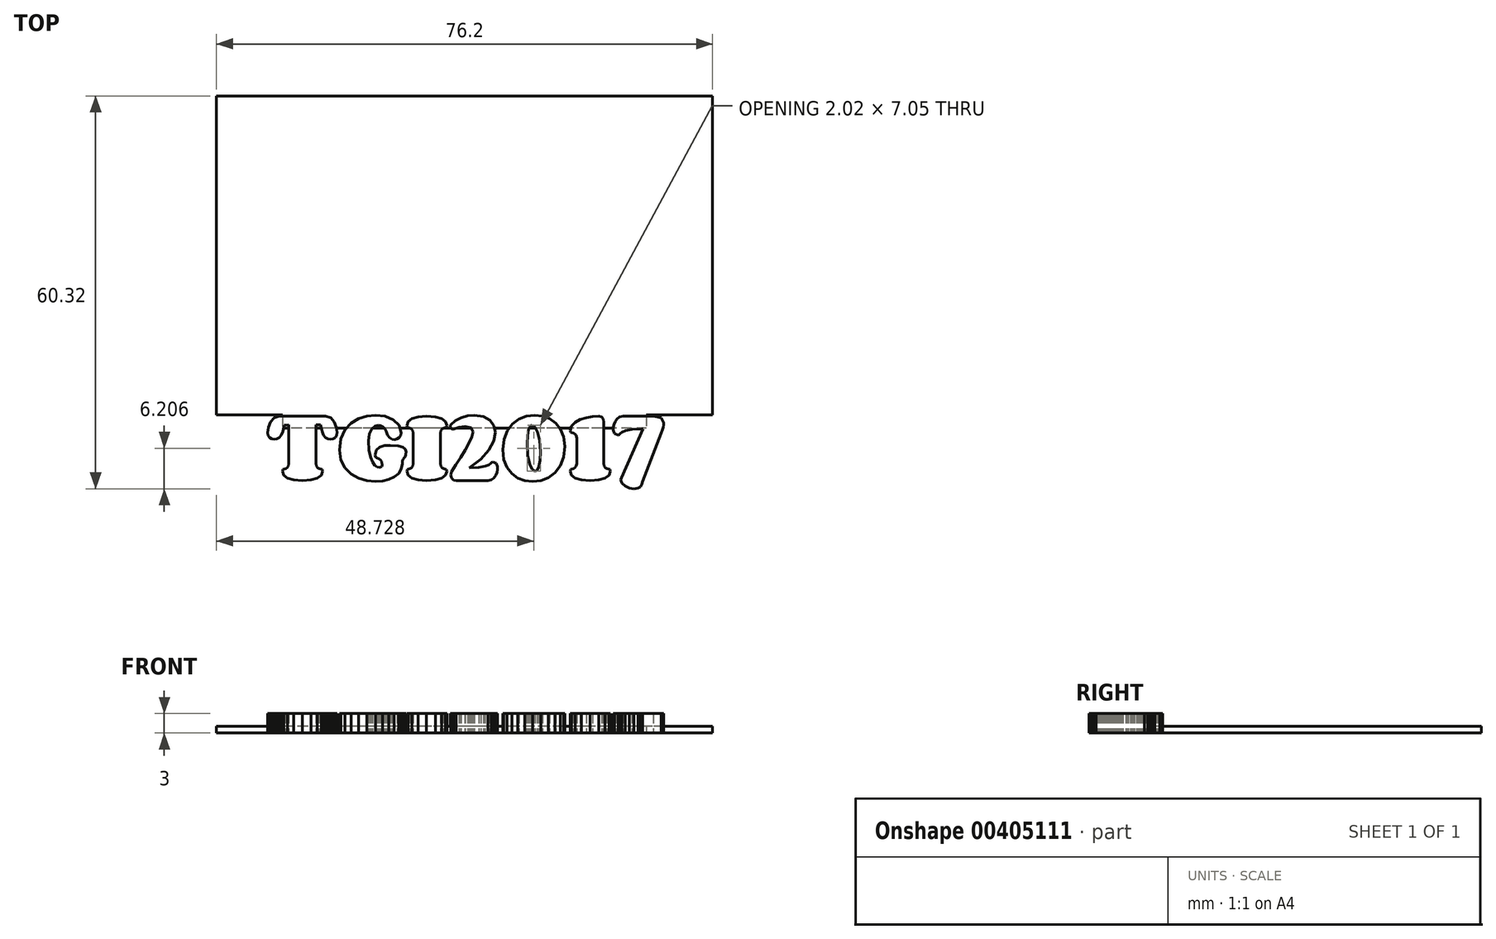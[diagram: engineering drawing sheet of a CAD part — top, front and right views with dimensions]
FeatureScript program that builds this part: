
annotation { "Feature Type Name" : "Feature", "Feature Type Description" : "" }
export const myFeature = defineFeature(function(context is Context, id is Id, definition is map)
    precondition{}
    {
        {
            var Q0;
            Q0=qCreatedBy(makeId("Top.planeOp"),FACE);
            var sketch = newSketch(context, id + "F0", { "sketchPlane" : qUnion([Q0])});
            skLineSegment(sketch, "E0.bottom", {"start": v(38.1, 24.5) * mm, "end": v(-38.1, 24.5) * mm});
            skLineSegment(sketch, "E0.top", {"start": v(38.1, -24.5) * mm, "end": v(-38.1, -24.5) * mm});
            skLineSegment(sketch, "E0.left", {"start": v(38.1, 24.5) * mm, "end": v(38.1, -24.5) * mm});
            skLineSegment(sketch, "E0.right", {"start": v(-38.1, 24.5) * mm, "end": v(-38.1, -24.5) * mm});
            skPoint(sketch, "E0.middle", {"position": v(0, 0) * mm});
            skPoint(sketch, "E1.middle", {"position": v(0, -24.5) * mm});
            skLineSegment(sketch, "E2.bottom", {"start": v(27.94, -22.5) * mm, "end": v(-27.94, -22.5) * mm});
            skLineSegment(sketch, "E2.top", {"start": v(27.94, -26.5) * mm, "end": v(-27.94, -26.5) * mm});
            skLineSegment(sketch, "E2.left", {"start": v(27.94, -22.5) * mm, "end": v(27.94, -26.5) * mm});
            skLineSegment(sketch, "E2.right", {"start": v(-27.94, -22.5) * mm, "end": v(-27.94, -26.5) * mm});
            skSolve(sketch);
        }
        {
            var Q0;
            Q0=makeQuery(id+"F0.imprint","IMPRINT",FACE,{"disambiguationData":[TD([[makeQuery(id+"F0.imprint","IMPRINT",EDGE,{"derivedFrom":sQuery(id+"F0.wireOp",EDGE,"E0.bottom")}),1.0]])]});
            var Q1;
            {var subQ5=sQuery(id+"F0.wireOp",EDGE,"E2.bottom");Q1=makeQuery(id+"F0.imprint","IMPRINT",FACE,{"disambiguationData":[TD([[makeQuery(id+"F0.imprint","IMPRINT",EDGE,{"derivedFrom":subQ5}),1.0]])]});}
            extrude(context, id + "F1", {"entities" : qUnion([Q0, Q1]), "depth" : 1 * mm});
        }
        {
            var Q0;
            {var subQ5=sQuery(id+"F0.wireOp",EDGE,"E2.top");Q0=makeQuery(id+"F0.imprint","IMPRINT",FACE,{"disambiguationData":[TD([[makeQuery(id+"F0.imprint","IMPRINT",EDGE,{"derivedFrom":subQ5}),-1.0]])]});}
            extrude(context, id + "F2", {"entities" : qUnion([Q0]), "operationType" : NewBodyOperationType.ADD, "depth" : 1 * mm});
        }
        {
            var Q0;
            Q0=qCreatedBy(makeId("Top.planeOp"),FACE);
            var sketch = newSketch(context, id + "F3", { "sketchPlane" : qUnion([Q0])});
            skLineSegment(sketch, "E3", {"start": v(-22.81, -31.93) * mm, "end": v(-22.74, -32.37) * mm});
            skLineSegment(sketch, "E4", {"start": v(-22.74, -32.37) * mm, "end": v(-22.56, -32.6) * mm});
            skLineSegment(sketch, "E5", {"start": v(-22.56, -32.6) * mm, "end": v(-22.31, -32.71) * mm});
            skLineSegment(sketch, "E6", {"start": v(-22.31, -32.71) * mm, "end": v(-22.07, -32.78) * mm});
            skLineSegment(sketch, "E7", {"start": v(-22.07, -32.78) * mm, "end": v(-21.89, -32.89) * mm});
            skLineSegment(sketch, "E8", {"start": v(-21.89, -32.89) * mm, "end": v(-21.81, -33.1) * mm});
            skLineSegment(sketch, "E9", {"start": v(-21.81, -33.1) * mm, "end": v(-22.01, -33.76) * mm});
            skLineSegment(sketch, "E10", {"start": v(-22.01, -33.76) * mm, "end": v(-22.6, -34.22) * mm});
            skLineSegment(sketch, "E11", {"start": v(-22.6, -34.22) * mm, "end": v(-23.6, -34.48) * mm});
            skLineSegment(sketch, "E12", {"start": v(-23.6, -34.48) * mm, "end": v(-24.93, -34.56) * mm});
            skLineSegment(sketch, "E13", {"start": v(-24.93, -34.56) * mm, "end": v(-26.22, -34.48) * mm});
            skLineSegment(sketch, "E14", {"start": v(-26.22, -34.48) * mm, "end": v(-27.18, -34.22) * mm});
            skLineSegment(sketch, "E15", {"start": v(-27.18, -34.22) * mm, "end": v(-27.77, -33.76) * mm});
            skLineSegment(sketch, "E16", {"start": v(-27.77, -33.76) * mm, "end": v(-27.97, -33.1) * mm});
            skLineSegment(sketch, "E17", {"start": v(-27.97, -33.1) * mm, "end": v(-27.9, -32.89) * mm});
            skLineSegment(sketch, "E18", {"start": v(-27.9, -32.89) * mm, "end": v(-27.71, -32.79) * mm});
            skLineSegment(sketch, "E19", {"start": v(-27.71, -32.79) * mm, "end": v(-27.48, -32.72) * mm});
            skLineSegment(sketch, "E20", {"start": v(-27.48, -32.72) * mm, "end": v(-27.24, -32.6) * mm});
            skLineSegment(sketch, "E21", {"start": v(-27.24, -32.6) * mm, "end": v(-27.06, -32.38) * mm});
            skLineSegment(sketch, "E22", {"start": v(-27.06, -32.38) * mm, "end": v(-26.98, -31.95) * mm});
            skLineSegment(sketch, "E23", {"start": v(-26.98, -31.95) * mm, "end": v(-26.98, -26.02) * mm});
            skLineSegment(sketch, "E24", {"start": v(-26.98, -26.02) * mm, "end": v(-27.68, -26.04) * mm});
            skLineSegment(sketch, "E25", {"start": v(-27.68, -26.04) * mm, "end": v(-27.92, -27.03) * mm});
            skLineSegment(sketch, "E26", {"start": v(-27.92, -27.03) * mm, "end": v(-28.16, -27.6) * mm});
            skLineSegment(sketch, "E27", {"start": v(-28.16, -27.6) * mm, "end": v(-28.48, -27.97) * mm});
            skLineSegment(sketch, "E28", {"start": v(-28.48, -27.97) * mm, "end": v(-28.83, -28.18) * mm});
            skLineSegment(sketch, "E29", {"start": v(-28.83, -28.18) * mm, "end": v(-29.2, -28.25) * mm});
            skLineSegment(sketch, "E30", {"start": v(-29.2, -28.25) * mm, "end": v(-29.61, -28.18) * mm});
            skLineSegment(sketch, "E31", {"start": v(-29.61, -28.18) * mm, "end": v(-29.94, -27.96) * mm});
            skLineSegment(sketch, "E32", {"start": v(-29.94, -27.96) * mm, "end": v(-30.16, -27.63) * mm});
            skLineSegment(sketch, "E33", {"start": v(-30.16, -27.63) * mm, "end": v(-30.23, -27.18) * mm});
            skLineSegment(sketch, "E34", {"start": v(-30.23, -27.18) * mm, "end": v(-30.12, -26.38) * mm});
            skLineSegment(sketch, "E35", {"start": v(-30.12, -26.38) * mm, "end": v(-29.8, -25.56) * mm});
            skLineSegment(sketch, "E36", {"start": v(-29.8, -25.56) * mm, "end": v(-29.24, -24.94) * mm});
            skLineSegment(sketch, "E37", {"start": v(-29.24, -24.94) * mm, "end": v(-28.45, -24.68) * mm});
            skLineSegment(sketch, "E38", {"start": v(-28.45, -24.68) * mm, "end": v(-21.34, -24.68) * mm});
            skLineSegment(sketch, "E39", {"start": v(-21.34, -24.68) * mm, "end": v(-20.55, -24.93) * mm});
            skLineSegment(sketch, "E40", {"start": v(-20.55, -24.93) * mm, "end": v(-20, -25.55) * mm});
            skLineSegment(sketch, "E41", {"start": v(-20, -25.55) * mm, "end": v(-19.68, -26.36) * mm});
            skLineSegment(sketch, "E42", {"start": v(-19.68, -26.36) * mm, "end": v(-19.57, -27.17) * mm});
            skLineSegment(sketch, "E43", {"start": v(-19.57, -27.17) * mm, "end": v(-19.64, -27.62) * mm});
            skLineSegment(sketch, "E44", {"start": v(-19.64, -27.62) * mm, "end": v(-19.86, -27.95) * mm});
            skLineSegment(sketch, "E45", {"start": v(-19.86, -27.95) * mm, "end": v(-20.18, -28.16) * mm});
            skLineSegment(sketch, "E46", {"start": v(-20.18, -28.16) * mm, "end": v(-20.59, -28.23) * mm});
            skLineSegment(sketch, "E47", {"start": v(-20.59, -28.23) * mm, "end": v(-20.97, -28.17) * mm});
            skLineSegment(sketch, "E48", {"start": v(-20.97, -28.17) * mm, "end": v(-21.34, -27.97) * mm});
            skLineSegment(sketch, "E49", {"start": v(-21.34, -27.97) * mm, "end": v(-21.66, -27.59) * mm});
            skLineSegment(sketch, "E50", {"start": v(-21.66, -27.59) * mm, "end": v(-21.87, -27.02) * mm});
            skLineSegment(sketch, "E51", {"start": v(-21.87, -27.02) * mm, "end": v(-22.11, -26.03) * mm});
            skLineSegment(sketch, "E52", {"start": v(-22.11, -26.03) * mm, "end": v(-22.81, -26) * mm});
            skLineSegment(sketch, "E53", {"start": v(-22.81, -26) * mm, "end": v(-22.81, -31.93) * mm});
            skLineSegment(sketch, "E54", {"start": v(-9.55, -31.95) * mm, "end": v(-9.7, -32.8) * mm});
            skLineSegment(sketch, "E55", {"start": v(-9.7, -32.8) * mm, "end": v(-10.14, -33.48) * mm});
            skLineSegment(sketch, "E56", {"start": v(-10.14, -33.48) * mm, "end": v(-10.8, -34.02) * mm});
            skLineSegment(sketch, "E57", {"start": v(-10.8, -34.02) * mm, "end": v(-11.64, -34.4) * mm});
            skLineSegment(sketch, "E58", {"start": v(-11.64, -34.4) * mm, "end": v(-12.6, -34.63) * mm});
            skLineSegment(sketch, "E59", {"start": v(-12.6, -34.63) * mm, "end": v(-13.66, -34.72) * mm});
            skLineSegment(sketch, "E60", {"start": v(-13.66, -34.72) * mm, "end": v(-14.98, -34.59) * mm});
            skLineSegment(sketch, "E61", {"start": v(-14.98, -34.59) * mm, "end": v(-16.27, -34.21) * mm});
            skLineSegment(sketch, "E62", {"start": v(-16.27, -34.21) * mm, "end": v(-17.43, -33.56) * mm});
            skLineSegment(sketch, "E63", {"start": v(-17.43, -33.56) * mm, "end": v(-18.37, -32.63) * mm});
            skLineSegment(sketch, "E64", {"start": v(-18.37, -32.63) * mm, "end": v(-19, -31.4) * mm});
            skLineSegment(sketch, "E65", {"start": v(-19, -31.4) * mm, "end": v(-19.23, -29.86) * mm});
            skLineSegment(sketch, "E66", {"start": v(-19.23, -29.86) * mm, "end": v(-19, -28.15) * mm});
            skLineSegment(sketch, "E67", {"start": v(-19, -28.15) * mm, "end": v(-18.37, -26.79) * mm});
            skLineSegment(sketch, "E68", {"start": v(-18.37, -26.79) * mm, "end": v(-17.44, -25.76) * mm});
            skLineSegment(sketch, "E69", {"start": v(-17.44, -25.76) * mm, "end": v(-16.29, -25.06) * mm});
            skLineSegment(sketch, "E70", {"start": v(-16.29, -25.06) * mm, "end": v(-15.01, -24.65) * mm});
            skLineSegment(sketch, "E71", {"start": v(-15.01, -24.65) * mm, "end": v(-13.7, -24.51) * mm});
            skLineSegment(sketch, "E72", {"start": v(-13.7, -24.51) * mm, "end": v(-12.2, -24.7) * mm});
            skLineSegment(sketch, "E73", {"start": v(-12.2, -24.7) * mm, "end": v(-10.93, -25.23) * mm});
            skLineSegment(sketch, "E74", {"start": v(-10.93, -25.23) * mm, "end": v(-10.06, -26.07) * mm});
            skLineSegment(sketch, "E75", {"start": v(-10.06, -26.07) * mm, "end": v(-9.73, -27.2) * mm});
            skLineSegment(sketch, "E76", {"start": v(-9.73, -27.2) * mm, "end": v(-9.8, -27.64) * mm});
            skLineSegment(sketch, "E77", {"start": v(-9.8, -27.64) * mm, "end": v(-10.03, -27.97) * mm});
            skLineSegment(sketch, "E78", {"start": v(-10.03, -27.97) * mm, "end": v(-10.35, -28.19) * mm});
            skLineSegment(sketch, "E79", {"start": v(-10.35, -28.19) * mm, "end": v(-10.76, -28.26) * mm});
            skLineSegment(sketch, "E80", {"start": v(-10.76, -28.26) * mm, "end": v(-11.15, -28.2) * mm});
            skLineSegment(sketch, "E81", {"start": v(-11.15, -28.2) * mm, "end": v(-11.51, -28) * mm});
            skLineSegment(sketch, "E82", {"start": v(-11.51, -28) * mm, "end": v(-11.82, -27.62) * mm});
            skLineSegment(sketch, "E83", {"start": v(-11.82, -27.62) * mm, "end": v(-12.04, -27.04) * mm});
            skLineSegment(sketch, "E84", {"start": v(-12.04, -27.04) * mm, "end": v(-12.23, -26.62) * mm});
            skLineSegment(sketch, "E85", {"start": v(-12.23, -26.62) * mm, "end": v(-12.55, -26.3) * mm});
            skLineSegment(sketch, "E86", {"start": v(-12.55, -26.3) * mm, "end": v(-12.91, -26.12) * mm});
            skLineSegment(sketch, "E87", {"start": v(-12.91, -26.12) * mm, "end": v(-13.25, -26.05) * mm});
            skLineSegment(sketch, "E88", {"start": v(-13.25, -26.05) * mm, "end": v(-13.74, -26.2) * mm});
            skLineSegment(sketch, "E89", {"start": v(-13.74, -26.2) * mm, "end": v(-14.23, -26.63) * mm});
            skLineSegment(sketch, "E90", {"start": v(-14.23, -26.63) * mm, "end": v(-14.6, -27.38) * mm});
            skLineSegment(sketch, "E91", {"start": v(-14.6, -27.38) * mm, "end": v(-14.76, -28.45) * mm});
            skLineSegment(sketch, "E92", {"start": v(-14.76, -28.45) * mm, "end": v(-14.68, -29.9) * mm});
            skLineSegment(sketch, "E93", {"start": v(-14.68, -29.9) * mm, "end": v(-14.45, -30.97) * mm});
            skLineSegment(sketch, "E94", {"start": v(-14.45, -30.97) * mm, "end": v(-14.14, -31.73) * mm});
            skLineSegment(sketch, "E95", {"start": v(-14.14, -31.73) * mm, "end": v(-13.78, -32.2) * mm});
            skLineSegment(sketch, "E96", {"start": v(-13.78, -32.2) * mm, "end": v(-13.4, -32.46) * mm});
            skLineSegment(sketch, "E97", {"start": v(-13.4, -32.46) * mm, "end": v(-13.06, -32.53) * mm});
            skLineSegment(sketch, "E98", {"start": v(-13.06, -32.53) * mm, "end": v(-12.75, -32.44) * mm});
            skLineSegment(sketch, "E99", {"start": v(-12.75, -32.44) * mm, "end": v(-12.62, -32.24) * mm});
            skLineSegment(sketch, "E100", {"start": v(-12.62, -32.24) * mm, "end": v(-12.71, -31.68) * mm});
            skLineSegment(sketch, "E101", {"start": v(-12.71, -31.68) * mm, "end": v(-12.92, -31.37) * mm});
            skLineSegment(sketch, "E102", {"start": v(-12.92, -31.37) * mm, "end": v(-13.2, -31.22) * mm});
            skLineSegment(sketch, "E103", {"start": v(-13.2, -31.22) * mm, "end": v(-13.47, -31.11) * mm});
            skLineSegment(sketch, "E104", {"start": v(-13.47, -31.11) * mm, "end": v(-13.67, -30.95) * mm});
            skLineSegment(sketch, "E105", {"start": v(-13.67, -30.95) * mm, "end": v(-13.76, -30.63) * mm});
            skLineSegment(sketch, "E106", {"start": v(-13.76, -30.63) * mm, "end": v(-13.56, -29.85) * mm});
            skLineSegment(sketch, "E107", {"start": v(-13.56, -29.85) * mm, "end": v(-13.03, -29.4) * mm});
            skLineSegment(sketch, "E108", {"start": v(-13.03, -29.4) * mm, "end": v(-12.28, -29.2) * mm});
            skLineSegment(sketch, "E109", {"start": v(-12.28, -29.2) * mm, "end": v(-11.4, -29.15) * mm});
            skLineSegment(sketch, "E110", {"start": v(-11.4, -29.15) * mm, "end": v(-10.21, -29.23) * mm});
            skLineSegment(sketch, "E111", {"start": v(-10.21, -29.23) * mm, "end": v(-9.46, -29.42) * mm});
            skLineSegment(sketch, "E112", {"start": v(-9.46, -29.42) * mm, "end": v(-9.08, -29.73) * mm});
            skLineSegment(sketch, "E113", {"start": v(-9.08, -29.73) * mm, "end": v(-8.97, -30.1) * mm});
            skLineSegment(sketch, "E114", {"start": v(-8.97, -30.1) * mm, "end": v(-9.01, -30.58) * mm});
            skLineSegment(sketch, "E115", {"start": v(-9.01, -30.58) * mm, "end": v(-9.12, -30.87) * mm});
            skLineSegment(sketch, "E116", {"start": v(-9.12, -30.87) * mm, "end": v(-9.26, -31.06) * mm});
            skLineSegment(sketch, "E117", {"start": v(-9.26, -31.06) * mm, "end": v(-9.4, -31.24) * mm});
            skLineSegment(sketch, "E118", {"start": v(-9.4, -31.24) * mm, "end": v(-9.51, -31.5) * mm});
            skLineSegment(sketch, "E119", {"start": v(-9.51, -31.5) * mm, "end": v(-9.55, -31.95) * mm});
            skLineSegment(sketch, "E120", {"start": v(-3.72, -31.93) * mm, "end": v(-3.65, -32.37) * mm});
            skLineSegment(sketch, "E121", {"start": v(-3.65, -32.37) * mm, "end": v(-3.46, -32.6) * mm});
            skLineSegment(sketch, "E122", {"start": v(-3.46, -32.6) * mm, "end": v(-3.22, -32.71) * mm});
            skLineSegment(sketch, "E123", {"start": v(-3.22, -32.71) * mm, "end": v(-2.98, -32.78) * mm});
            skLineSegment(sketch, "E124", {"start": v(-2.98, -32.78) * mm, "end": v(-2.8, -32.89) * mm});
            skLineSegment(sketch, "E125", {"start": v(-2.8, -32.89) * mm, "end": v(-2.72, -33.1) * mm});
            skLineSegment(sketch, "E126", {"start": v(-2.72, -33.1) * mm, "end": v(-2.92, -33.76) * mm});
            skLineSegment(sketch, "E127", {"start": v(-2.92, -33.76) * mm, "end": v(-3.52, -34.22) * mm});
            skLineSegment(sketch, "E128", {"start": v(-3.52, -34.22) * mm, "end": v(-4.5, -34.48) * mm});
            skLineSegment(sketch, "E129", {"start": v(-4.5, -34.48) * mm, "end": v(-5.83, -34.56) * mm});
            skLineSegment(sketch, "E130", {"start": v(-5.83, -34.56) * mm, "end": v(-7.13, -34.48) * mm});
            skLineSegment(sketch, "E131", {"start": v(-7.13, -34.48) * mm, "end": v(-8.09, -34.22) * mm});
            skLineSegment(sketch, "E132", {"start": v(-8.09, -34.22) * mm, "end": v(-8.68, -33.76) * mm});
            skLineSegment(sketch, "E133", {"start": v(-8.68, -33.76) * mm, "end": v(-8.87, -33.1) * mm});
            skLineSegment(sketch, "E134", {"start": v(-8.87, -33.1) * mm, "end": v(-8.8, -32.89) * mm});
            skLineSegment(sketch, "E135", {"start": v(-8.8, -32.89) * mm, "end": v(-8.62, -32.79) * mm});
            skLineSegment(sketch, "E136", {"start": v(-8.62, -32.79) * mm, "end": v(-8.38, -32.72) * mm});
            skLineSegment(sketch, "E137", {"start": v(-8.38, -32.72) * mm, "end": v(-8.15, -32.6) * mm});
            skLineSegment(sketch, "E138", {"start": v(-8.15, -32.6) * mm, "end": v(-7.96, -32.38) * mm});
            skLineSegment(sketch, "E139", {"start": v(-7.96, -32.38) * mm, "end": v(-7.89, -31.95) * mm});
            skLineSegment(sketch, "E140", {"start": v(-7.89, -31.95) * mm, "end": v(-7.89, -27.28) * mm});
            skLineSegment(sketch, "E141", {"start": v(-7.89, -27.28) * mm, "end": v(-7.96, -26.86) * mm});
            skLineSegment(sketch, "E142", {"start": v(-7.96, -26.86) * mm, "end": v(-8.15, -26.63) * mm});
            skLineSegment(sketch, "E143", {"start": v(-8.15, -26.63) * mm, "end": v(-8.38, -26.52) * mm});
            skLineSegment(sketch, "E144", {"start": v(-8.38, -26.52) * mm, "end": v(-8.62, -26.45) * mm});
            skLineSegment(sketch, "E145", {"start": v(-8.62, -26.45) * mm, "end": v(-8.8, -26.35) * mm});
            skLineSegment(sketch, "E146", {"start": v(-8.8, -26.35) * mm, "end": v(-8.87, -26.14) * mm});
            skLineSegment(sketch, "E147", {"start": v(-8.87, -26.14) * mm, "end": v(-8.68, -25.48) * mm});
            skLineSegment(sketch, "E148", {"start": v(-8.68, -25.48) * mm, "end": v(-8.09, -25.03) * mm});
            skLineSegment(sketch, "E149", {"start": v(-8.09, -25.03) * mm, "end": v(-7.13, -24.77) * mm});
            skLineSegment(sketch, "E150", {"start": v(-7.13, -24.77) * mm, "end": v(-5.83, -24.68) * mm});
            skLineSegment(sketch, "E151", {"start": v(-5.83, -24.68) * mm, "end": v(-4.5, -24.77) * mm});
            skLineSegment(sketch, "E152", {"start": v(-4.5, -24.77) * mm, "end": v(-3.52, -25.03) * mm});
            skLineSegment(sketch, "E153", {"start": v(-3.52, -25.03) * mm, "end": v(-2.92, -25.48) * mm});
            skLineSegment(sketch, "E154", {"start": v(-2.92, -25.48) * mm, "end": v(-2.72, -26.14) * mm});
            skLineSegment(sketch, "E155", {"start": v(-2.72, -26.14) * mm, "end": v(-2.8, -26.35) * mm});
            skLineSegment(sketch, "E156", {"start": v(-2.8, -26.35) * mm, "end": v(-2.98, -26.45) * mm});
            skLineSegment(sketch, "E157", {"start": v(-2.98, -26.45) * mm, "end": v(-3.21, -26.52) * mm});
            skLineSegment(sketch, "E158", {"start": v(-3.21, -26.52) * mm, "end": v(-3.46, -26.63) * mm});
            skLineSegment(sketch, "E159", {"start": v(-3.46, -26.63) * mm, "end": v(-3.64, -26.86) * mm});
            skLineSegment(sketch, "E160", {"start": v(-3.64, -26.86) * mm, "end": v(-3.7, -27.28) * mm});
            skLineSegment(sketch, "E161", {"start": v(-3.7, -27.28) * mm, "end": v(-3.72, -31.93) * mm});
            skLineSegment(sketch, "E162", {"start": v(-1.97, -33.17) * mm, "end": v(-1.33, -32.16) * mm});
            skLineSegment(sketch, "E163", {"start": v(-1.33, -32.16) * mm, "end": v(-0.62, -31.05) * mm});
            skLineSegment(sketch, "E164", {"start": v(-0.62, -31.05) * mm, "end": v(0.1, -29.9) * mm});
            skLineSegment(sketch, "E165", {"start": v(0.1, -29.9) * mm, "end": v(0.7, -28.8) * mm});
            skLineSegment(sketch, "E166", {"start": v(0.7, -28.8) * mm, "end": v(1.14, -27.83) * mm});
            skLineSegment(sketch, "E167", {"start": v(1.14, -27.83) * mm, "end": v(1.3, -27.06) * mm});
            skLineSegment(sketch, "E168", {"start": v(1.3, -27.06) * mm, "end": v(1.03, -26.47) * mm});
            skLineSegment(sketch, "E169", {"start": v(1.03, -26.47) * mm, "end": v(0.07, -26.26) * mm});
            skLineSegment(sketch, "E170", {"start": v(0.07, -26.26) * mm, "end": v(-0.85, -26.38) * mm});
            skLineSegment(sketch, "E171", {"start": v(-0.85, -26.38) * mm, "end": v(-1.6, -26.66) * mm});
            skLineSegment(sketch, "E172", {"start": v(-1.6, -26.66) * mm, "end": v(-1.8, -26.72) * mm});
            skLineSegment(sketch, "E173", {"start": v(-1.8, -26.72) * mm, "end": v(-1.95, -26.67) * mm});
            skLineSegment(sketch, "E174", {"start": v(-1.95, -26.67) * mm, "end": v(-2.07, -26.53) * mm});
            skLineSegment(sketch, "E175", {"start": v(-2.07, -26.53) * mm, "end": v(-2.15, -26.35) * mm});
            skLineSegment(sketch, "E176", {"start": v(-2.15, -26.35) * mm, "end": v(-2.18, -26.17) * mm});
            skLineSegment(sketch, "E177", {"start": v(-2.18, -26.17) * mm, "end": v(-2.16, -26.07) * mm});
            skLineSegment(sketch, "E178", {"start": v(-2.16, -26.07) * mm, "end": v(-2.11, -25.98) * mm});
            skLineSegment(sketch, "E179", {"start": v(-2.11, -25.98) * mm, "end": v(-1.4, -25.36) * mm});
            skLineSegment(sketch, "E180", {"start": v(-1.4, -25.36) * mm, "end": v(-0.51, -24.9) * mm});
            skLineSegment(sketch, "E181", {"start": v(-0.51, -24.9) * mm, "end": v(0.47, -24.63) * mm});
            skLineSegment(sketch, "E182", {"start": v(0.47, -24.63) * mm, "end": v(1.51, -24.53) * mm});
            skLineSegment(sketch, "E183", {"start": v(1.51, -24.53) * mm, "end": v(2.9, -24.73) * mm});
            skLineSegment(sketch, "E184", {"start": v(2.9, -24.73) * mm, "end": v(3.9, -25.28) * mm});
            skLineSegment(sketch, "E185", {"start": v(3.9, -25.28) * mm, "end": v(4.5, -26.11) * mm});
            skLineSegment(sketch, "E186", {"start": v(4.5, -26.11) * mm, "end": v(4.71, -27.16) * mm});
            skLineSegment(sketch, "E187", {"start": v(4.71, -27.16) * mm, "end": v(4.47, -28.46) * mm});
            skLineSegment(sketch, "E188", {"start": v(4.47, -28.46) * mm, "end": v(3.73, -29.85) * mm});
            skLineSegment(sketch, "E189", {"start": v(3.73, -29.85) * mm, "end": v(2.5, -31.27) * mm});
            skLineSegment(sketch, "E190", {"start": v(2.5, -31.27) * mm, "end": v(0.74, -32.6) * mm});
            skLineSegment(sketch, "E191", {"start": v(0.74, -32.6) * mm, "end": v(2.21, -32.53) * mm});
            skLineSegment(sketch, "E192", {"start": v(2.21, -32.53) * mm, "end": v(3.17, -32.36) * mm});
            skLineSegment(sketch, "E193", {"start": v(3.17, -32.36) * mm, "end": v(3.74, -32.15) * mm});
            skLineSegment(sketch, "E194", {"start": v(3.74, -32.15) * mm, "end": v(4.04, -31.93) * mm});
            skLineSegment(sketch, "E195", {"start": v(4.04, -31.93) * mm, "end": v(4.2, -31.76) * mm});
            skLineSegment(sketch, "E196", {"start": v(4.2, -31.76) * mm, "end": v(4.34, -31.69) * mm});
            skLineSegment(sketch, "E197", {"start": v(4.34, -31.69) * mm, "end": v(4.87, -31.9) * mm});
            skLineSegment(sketch, "E198", {"start": v(4.87, -31.9) * mm, "end": v(5.08, -32.44) * mm});
            skLineSegment(sketch, "E199", {"start": v(5.08, -32.44) * mm, "end": v(5.06, -32.84) * mm});
            skLineSegment(sketch, "E200", {"start": v(5.06, -32.84) * mm, "end": v(4.97, -33.3) * mm});
            skLineSegment(sketch, "E201", {"start": v(4.97, -33.3) * mm, "end": v(4.8, -33.76) * mm});
            skLineSegment(sketch, "E202", {"start": v(4.8, -33.76) * mm, "end": v(4.51, -34.17) * mm});
            skLineSegment(sketch, "E203", {"start": v(4.51, -34.17) * mm, "end": v(4.12, -34.46) * mm});
            skLineSegment(sketch, "E204", {"start": v(4.12, -34.46) * mm, "end": v(3.58, -34.56) * mm});
            skLineSegment(sketch, "E205", {"start": v(3.58, -34.56) * mm, "end": v(-1.27, -34.56) * mm});
            skLineSegment(sketch, "E206", {"start": v(-1.27, -34.56) * mm, "end": v(-1.65, -34.48) * mm});
            skLineSegment(sketch, "E207", {"start": v(-1.65, -34.48) * mm, "end": v(-1.92, -34.29) * mm});
            skLineSegment(sketch, "E208", {"start": v(-1.92, -34.29) * mm, "end": v(-2.07, -34) * mm});
            skLineSegment(sketch, "E209", {"start": v(-2.07, -34) * mm, "end": v(-2.11, -33.68) * mm});
            skLineSegment(sketch, "E210", {"start": v(-2.11, -33.68) * mm, "end": v(-2.07, -33.4) * mm});
            skLineSegment(sketch, "E211", {"start": v(-2.07, -33.4) * mm, "end": v(-1.97, -33.17) * mm});
            skLineSegment(sketch, "E212", {"start": v(15.4, -29.3) * mm, "end": v(15.21, -30.96) * mm});
            skLineSegment(sketch, "E213", {"start": v(15.21, -30.96) * mm, "end": v(14.7, -32.32) * mm});
            skLineSegment(sketch, "E214", {"start": v(14.7, -32.32) * mm, "end": v(13.9, -33.37) * mm});
            skLineSegment(sketch, "E215", {"start": v(13.9, -33.37) * mm, "end": v(12.9, -34.12) * mm});
            skLineSegment(sketch, "E216", {"start": v(12.9, -34.12) * mm, "end": v(11.73, -34.57) * mm});
            skLineSegment(sketch, "E217", {"start": v(11.73, -34.57) * mm, "end": v(10.48, -34.72) * mm});
            skLineSegment(sketch, "E218", {"start": v(10.48, -34.72) * mm, "end": v(9.28, -34.58) * mm});
            skLineSegment(sketch, "E219", {"start": v(9.28, -34.58) * mm, "end": v(8.19, -34.18) * mm});
            skLineSegment(sketch, "E220", {"start": v(8.19, -34.18) * mm, "end": v(7.25, -33.5) * mm});
            skLineSegment(sketch, "E221", {"start": v(7.25, -33.5) * mm, "end": v(6.52, -32.54) * mm});
            skLineSegment(sketch, "E222", {"start": v(6.52, -32.54) * mm, "end": v(6.04, -31.33) * mm});
            skLineSegment(sketch, "E223", {"start": v(6.04, -31.33) * mm, "end": v(5.87, -29.84) * mm});
            skLineSegment(sketch, "E224", {"start": v(5.87, -29.84) * mm, "end": v(6.06, -28.21) * mm});
            skLineSegment(sketch, "E225", {"start": v(6.06, -28.21) * mm, "end": v(6.57, -26.88) * mm});
            skLineSegment(sketch, "E226", {"start": v(6.57, -26.88) * mm, "end": v(7.36, -25.85) * mm});
            skLineSegment(sketch, "E227", {"start": v(7.36, -25.85) * mm, "end": v(8.35, -25.11) * mm});
            skLineSegment(sketch, "E228", {"start": v(8.35, -25.11) * mm, "end": v(9.5, -24.68) * mm});
            skLineSegment(sketch, "E229", {"start": v(9.5, -24.68) * mm, "end": v(10.76, -24.53) * mm});
            skLineSegment(sketch, "E230", {"start": v(10.76, -24.53) * mm, "end": v(11.95, -24.66) * mm});
            skLineSegment(sketch, "E231", {"start": v(11.95, -24.66) * mm, "end": v(13.06, -25.06) * mm});
            skLineSegment(sketch, "E232", {"start": v(13.06, -25.06) * mm, "end": v(14, -25.74) * mm});
            skLineSegment(sketch, "E233", {"start": v(14, -25.74) * mm, "end": v(14.74, -26.66) * mm});
            skLineSegment(sketch, "E234", {"start": v(14.74, -26.66) * mm, "end": v(15.22, -27.85) * mm});
            skLineSegment(sketch, "E235", {"start": v(15.22, -27.85) * mm, "end": v(15.4, -29.3) * mm});
            skLineSegment(sketch, "E236", {"start": v(9.62, -28.91) * mm, "end": v(9.72, -30.68) * mm});
            skLineSegment(sketch, "E237", {"start": v(9.72, -30.68) * mm, "end": v(10, -32) * mm});
            skLineSegment(sketch, "E238", {"start": v(10, -32) * mm, "end": v(10.4, -32.85) * mm});
            skLineSegment(sketch, "E239", {"start": v(10.4, -32.85) * mm, "end": v(10.84, -33.14) * mm});
            skLineSegment(sketch, "E240", {"start": v(10.84, -33.14) * mm, "end": v(11.14, -32.96) * mm});
            skLineSegment(sketch, "E241", {"start": v(11.14, -32.96) * mm, "end": v(11.4, -32.42) * mm});
            skLineSegment(sketch, "E242", {"start": v(11.4, -32.42) * mm, "end": v(11.57, -31.48) * mm});
            skLineSegment(sketch, "E243", {"start": v(11.57, -31.48) * mm, "end": v(11.64, -30.11) * mm});
            skLineSegment(sketch, "E244", {"start": v(11.64, -30.11) * mm, "end": v(11.52, -28.44) * mm});
            skLineSegment(sketch, "E245", {"start": v(11.52, -28.44) * mm, "end": v(11.24, -27.17) * mm});
            skLineSegment(sketch, "E246", {"start": v(11.24, -27.17) * mm, "end": v(10.85, -26.37) * mm});
            skLineSegment(sketch, "E247", {"start": v(10.85, -26.37) * mm, "end": v(10.42, -26.09) * mm});
            skLineSegment(sketch, "E248", {"start": v(10.42, -26.09) * mm, "end": v(10.1, -26.25) * mm});
            skLineSegment(sketch, "E249", {"start": v(10.1, -26.25) * mm, "end": v(9.85, -26.77) * mm});
            skLineSegment(sketch, "E250", {"start": v(9.85, -26.77) * mm, "end": v(9.68, -27.65) * mm});
            skLineSegment(sketch, "E251", {"start": v(9.68, -27.65) * mm, "end": v(9.62, -28.91) * mm});
            skLineSegment(sketch, "E252", {"start": v(21.4, -31.93) * mm, "end": v(21.46, -32.37) * mm});
            skLineSegment(sketch, "E253", {"start": v(21.46, -32.37) * mm, "end": v(21.65, -32.6) * mm});
            skLineSegment(sketch, "E254", {"start": v(21.65, -32.6) * mm, "end": v(21.9, -32.71) * mm});
            skLineSegment(sketch, "E255", {"start": v(21.9, -32.71) * mm, "end": v(22.13, -32.78) * mm});
            skLineSegment(sketch, "E256", {"start": v(22.13, -32.78) * mm, "end": v(22.32, -32.89) * mm});
            skLineSegment(sketch, "E257", {"start": v(22.32, -32.89) * mm, "end": v(22.4, -33.1) * mm});
            skLineSegment(sketch, "E258", {"start": v(22.4, -33.1) * mm, "end": v(22.2, -33.76) * mm});
            skLineSegment(sketch, "E259", {"start": v(22.2, -33.76) * mm, "end": v(21.6, -34.22) * mm});
            skLineSegment(sketch, "E260", {"start": v(21.6, -34.22) * mm, "end": v(20.62, -34.48) * mm});
            skLineSegment(sketch, "E261", {"start": v(20.62, -34.48) * mm, "end": v(19.29, -34.56) * mm});
            skLineSegment(sketch, "E262", {"start": v(19.29, -34.56) * mm, "end": v(17.98, -34.48) * mm});
            skLineSegment(sketch, "E263", {"start": v(17.98, -34.48) * mm, "end": v(17.03, -34.22) * mm});
            skLineSegment(sketch, "E264", {"start": v(17.03, -34.22) * mm, "end": v(16.44, -33.76) * mm});
            skLineSegment(sketch, "E265", {"start": v(16.44, -33.76) * mm, "end": v(16.24, -33.1) * mm});
            skLineSegment(sketch, "E266", {"start": v(16.24, -33.1) * mm, "end": v(16.31, -32.89) * mm});
            skLineSegment(sketch, "E267", {"start": v(16.31, -32.89) * mm, "end": v(16.5, -32.79) * mm});
            skLineSegment(sketch, "E268", {"start": v(16.5, -32.79) * mm, "end": v(16.73, -32.72) * mm});
            skLineSegment(sketch, "E269", {"start": v(16.73, -32.72) * mm, "end": v(16.96, -32.6) * mm});
            skLineSegment(sketch, "E270", {"start": v(16.96, -32.6) * mm, "end": v(17.15, -32.38) * mm});
            skLineSegment(sketch, "E271", {"start": v(17.15, -32.38) * mm, "end": v(17.22, -31.95) * mm});
            skLineSegment(sketch, "E272", {"start": v(17.22, -31.95) * mm, "end": v(17.22, -28.05) * mm});
            skLineSegment(sketch, "E273", {"start": v(17.22, -28.05) * mm, "end": v(17.15, -27.62) * mm});
            skLineSegment(sketch, "E274", {"start": v(17.15, -27.62) * mm, "end": v(16.96, -27.39) * mm});
            skLineSegment(sketch, "E275", {"start": v(16.96, -27.39) * mm, "end": v(16.73, -27.29) * mm});
            skLineSegment(sketch, "E276", {"start": v(16.73, -27.29) * mm, "end": v(16.5, -27.22) * mm});
            skLineSegment(sketch, "E277", {"start": v(16.5, -27.22) * mm, "end": v(16.31, -27.12) * mm});
            skLineSegment(sketch, "E278", {"start": v(16.31, -27.12) * mm, "end": v(16.24, -26.9) * mm});
            skLineSegment(sketch, "E279", {"start": v(16.24, -26.9) * mm, "end": v(16.45, -26.2) * mm});
            skLineSegment(sketch, "E280", {"start": v(16.45, -26.2) * mm, "end": v(17, -25.63) * mm});
            skLineSegment(sketch, "E281", {"start": v(17, -25.63) * mm, "end": v(17.79, -25.2) * mm});
            skLineSegment(sketch, "E282", {"start": v(17.79, -25.2) * mm, "end": v(18.72, -24.92) * mm});
            skLineSegment(sketch, "E283", {"start": v(18.72, -24.92) * mm, "end": v(19.69, -24.75) * mm});
            skLineSegment(sketch, "E284", {"start": v(19.69, -24.75) * mm, "end": v(20.6, -24.7) * mm});
            skLineSegment(sketch, "E285", {"start": v(20.6, -24.7) * mm, "end": v(21.05, -24.8) * mm});
            skLineSegment(sketch, "E286", {"start": v(21.05, -24.8) * mm, "end": v(21.3, -25.1) * mm});
            skLineSegment(sketch, "E287", {"start": v(21.3, -25.1) * mm, "end": v(21.4, -25.6) * mm});
            skLineSegment(sketch, "E288", {"start": v(21.4, -25.6) * mm, "end": v(21.4, -26.27) * mm});
            skLineSegment(sketch, "E289", {"start": v(21.4, -26.27) * mm, "end": v(21.4, -31.93) * mm});
            skLineSegment(sketch, "E290", {"start": v(27.19, -26.66) * mm, "end": v(25.72, -26.73) * mm});
            skLineSegment(sketch, "E291", {"start": v(25.72, -26.73) * mm, "end": v(24.76, -26.9) * mm});
            skLineSegment(sketch, "E292", {"start": v(24.76, -26.9) * mm, "end": v(24.2, -27.11) * mm});
            skLineSegment(sketch, "E293", {"start": v(24.2, -27.11) * mm, "end": v(23.9, -27.33) * mm});
            skLineSegment(sketch, "E294", {"start": v(23.9, -27.33) * mm, "end": v(23.73, -27.5) * mm});
            skLineSegment(sketch, "E295", {"start": v(23.73, -27.5) * mm, "end": v(23.6, -27.57) * mm});
            skLineSegment(sketch, "E296", {"start": v(23.6, -27.57) * mm, "end": v(23.06, -27.36) * mm});
            skLineSegment(sketch, "E297", {"start": v(23.06, -27.36) * mm, "end": v(22.85, -26.82) * mm});
            skLineSegment(sketch, "E298", {"start": v(22.85, -26.82) * mm, "end": v(22.87, -26.41) * mm});
            skLineSegment(sketch, "E299", {"start": v(22.87, -26.41) * mm, "end": v(22.96, -25.96) * mm});
            skLineSegment(sketch, "E300", {"start": v(22.96, -25.96) * mm, "end": v(23.14, -25.5) * mm});
            skLineSegment(sketch, "E301", {"start": v(23.14, -25.5) * mm, "end": v(23.41, -25.1) * mm});
            skLineSegment(sketch, "E302", {"start": v(23.41, -25.1) * mm, "end": v(23.81, -24.8) * mm});
            skLineSegment(sketch, "E303", {"start": v(23.81, -24.8) * mm, "end": v(24.35, -24.7) * mm});
            skLineSegment(sketch, "E304", {"start": v(24.35, -24.7) * mm, "end": v(29.03, -24.7) * mm});
            skLineSegment(sketch, "E305", {"start": v(29.03, -24.7) * mm, "end": v(30.23, -24.93) * mm});
            skLineSegment(sketch, "E306", {"start": v(30.23, -24.93) * mm, "end": v(30.6, -25.7) * mm});
            skLineSegment(sketch, "E307", {"start": v(30.6, -25.7) * mm, "end": v(30.57, -26) * mm});
            skLineSegment(sketch, "E308", {"start": v(30.57, -26) * mm, "end": v(30.5, -26.35) * mm});
            skLineSegment(sketch, "E309", {"start": v(30.5, -26.35) * mm, "end": v(30.38, -26.77) * mm});
            skLineSegment(sketch, "E310", {"start": v(30.38, -26.77) * mm, "end": v(30.2, -27.3) * mm});
            skLineSegment(sketch, "E311", {"start": v(30.2, -27.3) * mm, "end": v(27.37, -34.7) * mm});
            skLineSegment(sketch, "E312", {"start": v(27.37, -34.7) * mm, "end": v(27.2, -35.17) * mm});
            skLineSegment(sketch, "E313", {"start": v(27.2, -35.17) * mm, "end": v(27, -35.52) * mm});
            skLineSegment(sketch, "E314", {"start": v(27, -35.52) * mm, "end": v(26.66, -35.74) * mm});
            skLineSegment(sketch, "E315", {"start": v(26.66, -35.74) * mm, "end": v(26.05, -35.82) * mm});
            skLineSegment(sketch, "E316", {"start": v(26.05, -35.82) * mm, "end": v(25.33, -35.7) * mm});
            skLineSegment(sketch, "E317", {"start": v(25.33, -35.7) * mm, "end": v(24.68, -35.41) * mm});
            skLineSegment(sketch, "E318", {"start": v(24.68, -35.41) * mm, "end": v(24.2, -34.97) * mm});
            skLineSegment(sketch, "E319", {"start": v(24.2, -34.97) * mm, "end": v(24, -34.45) * mm});
            skLineSegment(sketch, "E320", {"start": v(24, -34.45) * mm, "end": v(24.09, -34.11) * mm});
            skLineSegment(sketch, "E321", {"start": v(24.09, -34.11) * mm, "end": v(27.43, -26.65) * mm});
            skLineSegment(sketch, "E322", {"start": v(27.43, -26.65) * mm, "end": v(27.19, -26.66) * mm});
            skSolve(sketch);
        }
        {
            var Q0;
            Q0=qSketchRegion(id+"F3",true);
            extrude(context, id + "F4", {"entities" : qUnion([Q0]), "depth" : 3 * mm});
        }
    });
